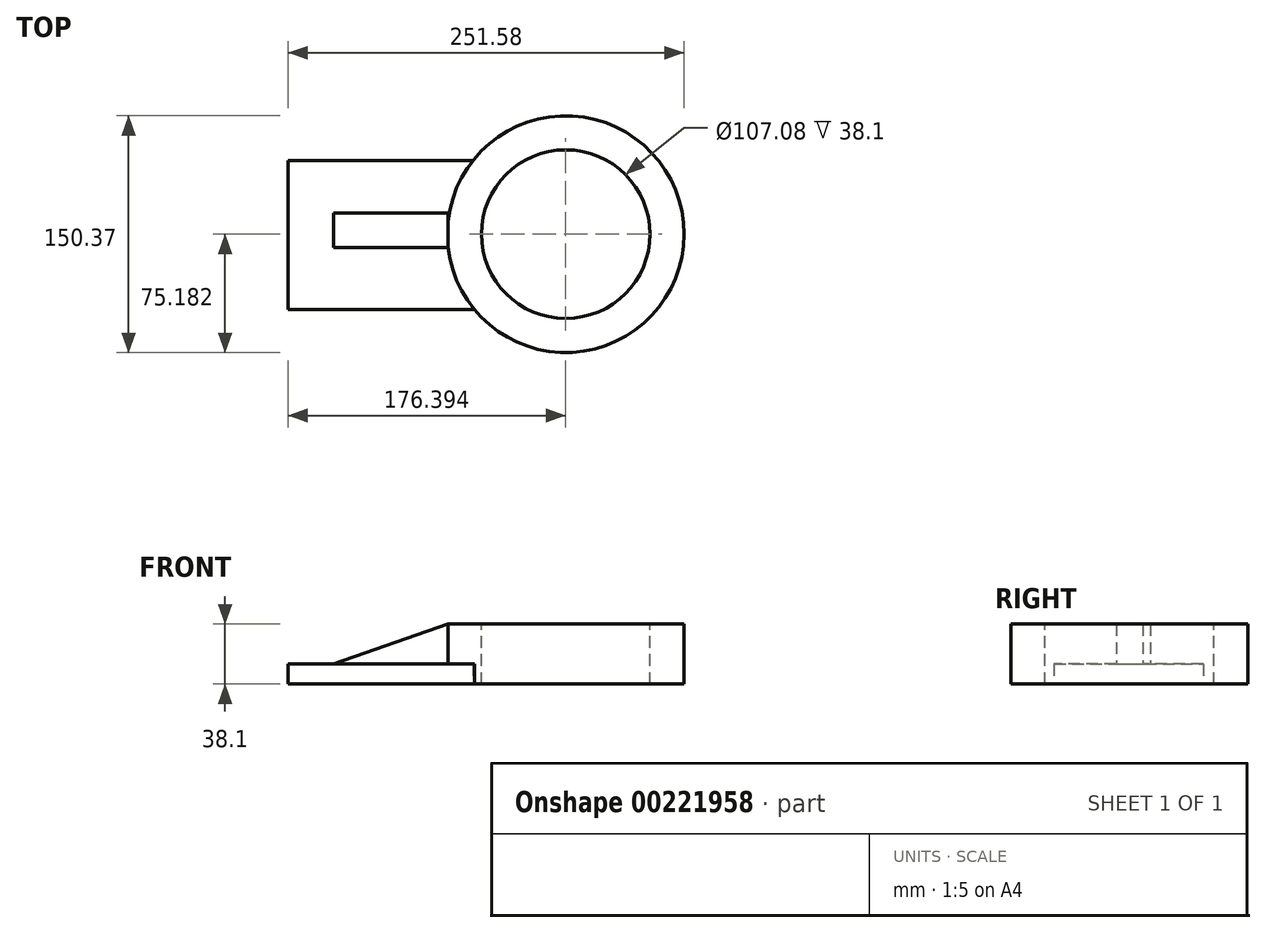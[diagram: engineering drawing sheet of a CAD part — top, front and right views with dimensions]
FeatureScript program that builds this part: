
annotation { "Feature Type Name" : "Feature", "Feature Type Description" : "" }
export const myFeature = defineFeature(function(context is Context, id is Id, definition is map)
    precondition{}
    {
        {
            var Q0;
            Q0=qCreatedBy(makeId("Top.planeOp"),FACE);
            var sketch = newSketch(context, id + "F0", { "sketchPlane" : qUnion([Q0])});
            skLineSegment(sketch, "E0", {"start": v(47.9, 55.21) * mm, "end": v(47.9, -39.51) * mm});
            skLineSegment(sketch, "E1", {"start": v(47.9, -39.51) * mm, "end": v(-110.95, -39.51) * mm});
            skLineSegment(sketch, "E2", {"start": v(-110.95, -39.51) * mm, "end": v(-110.95, 55.21) * mm});
            skLineSegment(sketch, "E3", {"start": v(-110.95, 55.21) * mm, "end": v(47.9, 55.21) * mm});
            skSolve(sketch);
        }
        {
            var Q0;
            Q0 = qSketchRegion(id + "F0", true);
            extrude(context, id + "F1", {"entities" : qUnion([Q0]), "depth" : 12.7 * mm});
        }
        {
            var Q0;
            Q0=makeQuery(id+"F1.opExtrude","CAP_FACE",FACE,{"disambiguationData":[OSD([sQuery(id+"F0.wireOp",EDGE,"E0"),sQuery(id+"F0.wireOp",EDGE,"E1"),sQuery(id+"F0.wireOp",EDGE,"E2"),sQuery(id+"F0.wireOp",EDGE,"E3")])],"isStart":false});
            var sketch = newSketch(context, id + "F2", { "sketchPlane" : qUnion([Q0])});
            skArc(sketch, "E4", {"start": v(47.9, 55.21) * mm, "mid": v(16.2, 7.85) * mm, "end": v(47.9, -39.51) * mm});
            skLineSegment(sketch, "E5", {"start": v(47.9, -39.51) * mm, "end": v(47.9, 55.21) * mm});
            skSolve(sketch);
        }
        {
            var Q0;
            Q0 = qSketchRegion(id + "F2", true);
            extrude(context, id + "F3", {"entities" : qUnion([Q0]), "operationType" : NewBodyOperationType.REMOVE, "endBound" : BoundingType.THROUGH_ALL, "oppositeDirection" : true, "depth" : 25.4 * mm});
        }
        {
            var Q0;
            Q0=qCreatedBy(makeId("Top.planeOp"),FACE);
            var sketch = newSketch(context, id + "F4", { "sketchPlane" : qUnion([Q0])});
            skCircle(sketch, "E6", {"center": v(65.44, 8.41) * mm, "radius": 75.18 * mm});
            skSolve(sketch);
        }
        {
            var Q0;
            Q0 = qSketchRegion(id + "F4", true);
            extrude(context, id + "F5", {"entities" : qUnion([Q0]), "operationType" : NewBodyOperationType.ADD, "depth" : 38.1 * mm});
        }
        {
            var Q0;
            Q0=makeQuery(id+"F5.opExtrude","CAP_FACE",FACE,{"disambiguationData":[OSD([sQuery(id+"F4.wireOp",EDGE,"E6")])],"isStart":false});
            var sketch = newSketch(context, id + "F6", { "sketchPlane" : qUnion([Q0])});
            skCircle(sketch, "E7", {"center": v(65.44, 8.41) * mm, "radius": 53.54 * mm});
            skSolve(sketch);
        }
        {
            var Q0;
            Q0 = qSketchRegion(id + "F6", true);
            extrude(context, id + "F7", {"entities" : qUnion([Q0]), "operationType" : NewBodyOperationType.REMOVE, "endBound" : BoundingType.THROUGH_ALL, "oppositeDirection" : true, "depth" : 25.4 * mm});
        }
        {
            var Q0;
            Q0=makeQuery(id+"F1.opExtrude","CAP_FACE",FACE,{"disambiguationData":[OSD([sQuery(id+"F0.wireOp",EDGE,"E0"),sQuery(id+"F0.wireOp",EDGE,"E1"),sQuery(id+"F0.wireOp",EDGE,"E2"),sQuery(id+"F0.wireOp",EDGE,"E3")])],"isStart":false});
            var sketch = newSketch(context, id + "F8", { "sketchPlane" : qUnion([Q0])});
            skLineSegment(sketch, "E8.bottom", {"start": v(-9.27, 0) * mm, "end": v(-81.9, 0) * mm});
            skLineSegment(sketch, "E8.top", {"start": v(-9.27, 21.69) * mm, "end": v(-81.9, 21.69) * mm});
            skLineSegment(sketch, "E8.left", {"start": v(-9.27, 0) * mm, "end": v(-9.27, 21.69) * mm});
            skLineSegment(sketch, "E8.right", {"start": v(-81.9, 0) * mm, "end": v(-81.9, 21.69) * mm});
            skSolve(sketch);
        }
        {
            var Q0;
            Q0 = qSketchRegion(id + "F8", true);
            extrude(context, id + "F9", {"entities" : qUnion([Q0]), "operationType" : NewBodyOperationType.ADD, "depth" : 25.4 * mm});
        }
        {
            var Q0;
            Q0=makeQuery(id+"F9.opExtrude","SWEPT_FACE",FACE,{"disambiguationData":[OSD([sQuery(id+"F8.wireOp",EDGE,"E8.bottom")])]});
            var sketch = newSketch(context, id + "F10", { "sketchPlane" : qUnion([Q0])});
            skLineSegment(sketch, "E9", {"start": v(-81.9, 12.7) * mm, "end": v(-9.27, 38.1) * mm});
            skLineSegment(sketch, "E10", {"start": v(-9.27, 38.1) * mm, "end": v(-81.9, 38.1) * mm});
            skLineSegment(sketch, "E11", {"start": v(-81.9, 38.1) * mm, "end": v(-81.9, 12.7) * mm});
            skSolve(sketch);
        }
        {
            var Q0;
            Q0 = qSketchRegion(id + "F10", true);
            extrude(context, id + "F11", {"entities" : qUnion([Q0]), "operationType" : NewBodyOperationType.REMOVE, "endBound" : BoundingType.THROUGH_ALL, "oppositeDirection" : true, "depth" : 25.4 * mm});
        }
    });
